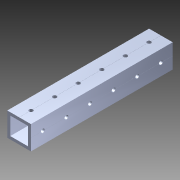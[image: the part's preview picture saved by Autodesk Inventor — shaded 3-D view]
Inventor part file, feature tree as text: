
AUTODESK INVENTOR PART (.ipt)
format: ipt  version: 2014 (Build 180170000, 170)  size: 1,135,104 bytes
history: native  units: in
note: dims shown in document units (in); Inventor stores cm internally (conversion verified against a paired STEP export)
features: pattern_circular x1, other x1, plane x1, extrude x1, imported_body x1, sketch x1
ambient origin geometry x8: Origin, YZ Plane, XZ Plane, XY Plane, X Axis, Y Axis, Z Axis, Center Point
bodies: Body1 (feature_tree)
feature tree (6):
  pattern_circular  "CirPattern2"
  other  "217-3426-STEP1"
  plane  "Work Plane1"
  extrude  "Extrusion1"  Depth=3937.0079in TaperAngle=0.0deg
  imported_body  "Base1"
  sketch  "Sketch1"  dims[d0=-6.0in d1=3937.0079in d2=0.0in]
